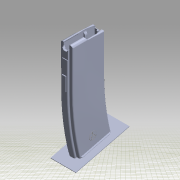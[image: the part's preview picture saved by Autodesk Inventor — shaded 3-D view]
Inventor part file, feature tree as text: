
AUTODESK INVENTOR PART (.ipt)
format: ipt  version: 2018 (Build 220112000, 112)  size: 2,089,472 bytes
history: native  units: mm (DEFAULTED — no unit token found)
features: sketch x7, extrude x7, mirror x5, projected_geometry x3, plane x2, fillet x1, imported_body x1
ambient origin geometry x8: Origin, YZ Plane, XZ Plane, XY Plane, X Axis, Y Axis, Z Axis, Center Point
bodies: Solid2 (feature_tree), Solid1 (feature_tree), Solid3 (feature_tree)
feature tree (26):
  sketch  "Sketch1"  dims[d0=1.0mm d1=0.0mm d2=1.0mm d3=0.0mm]
  extrude  "Extrusion1"  Depth=1.0mm TaperAngle=0.0deg
  plane  "Work Plane1"
  mirror  "Mirror1"
  extrude  "Extrusion2"  Depth=10.0mm TaperAngle=0.0deg
  plane  "Work Plane2"
  extrude  "Extrusion3"  Depth=0.1mm TaperAngle=0.0deg
  fillet  "Fillet1"  Radius=10.0mm
  extrude  "Extrusion4"  Depth=10.0mm TaperAngle=0.0deg
  mirror  "Mirror2"
  mirror  "Mirror3"
  extrude  "Extrusion5"  [1 undecoded]
  mirror  "Mirror4"
  extrude  "Extrusion6"  [1 undecoded]
  extrude  "Extrusion7"  [1 undecoded]
  imported_body  "Base2"
  mirror  "Mirror5"
  sketch  "Sketch2"  dims[d4=-14.56mm d5=10.0mm d6=0.0mm]
  sketch  "Sketch5"  dims[d7=7.0mm d8=0.1mm d9=0.0mm d10=10.0mm d11=0.0mm]
  projected_geometry  "Projected Loop2"
  sketch  "Sketch6"  dims[d12=10.0mm d13=0.0mm d14=10.0mm d15=0.0mm]
  projected_geometry  "Projected Loop4"
  sketch  "Sketch7"
  sketch  "Sketch8"
  projected_geometry  "Projected Loop5"
  sketch  "Sketch9"
note: 3 required parameter values undecoded (feature->parameter linkage not recoverable at this tier; creation-order binding heuristic only, values carry confidence <= 0.55)
